# Revit family: Plumbing-Flushometer-Sloan-Valve-Sloan-186_
name_source: partatom
category: Plumbing Fixtures
units: mm (PartAtom-declared; Revit-internal decimal feet)

## family parameters
Cut with Voids When Loaded = No
Host = Face
OmniClass Number = 23.45.05.14.99
OmniClass Title = Other Sanitary Washing Plumbing Fixtures
Part Type = Normal
Room Calculation Point = No
Round Connector Dimension = Use Diameter
Shared = No

## types (22) — shared parameters
Assembly Code = D2020300
CW Connection = Yes
Centerline of Supply from Top of Fixture = 11 1/2"
Centerline of Supply to Centerline of Valve = 4 3/4"
Default Elevation = 0"
Edition number = 1
HW Connection = No
Height = 13 3/4"
Keynote = 15410
Manufacturer = Sloan Valve
Operating Water Pressure = 15 – 80 PSI (103 – 552 kPa)
Product Material = Sloan Valve - Finish - Polished Chrome
Product data url = https://bimobject.com
URL = www.sloanvalve.com
Valve Pressure Drop = 0.00 psi
Vent Connection = No
Waste Connection = No
Water Inlet Connection Diameter = 1"
zero-valued in all types: CWFU, HWFU, WFU

## per-type parameters (varying)
| type | Description | Flush Rate | Part Number |
| SLOAN 186-1.0-YJ | 1.0 gpf, Polished Chrome Finish, Fixture Connection Top Spud, Single Flush, Split Ring Pipe Support, Sloan® Exposed Manual Urinal Flushometer. | 1.0 gpf (3.8 Lpf) | 3782627 |
| SLOAN 186-1.0-YBC | 1.0 gpf, Cast Set Screw Wall Flange, Polished Chrome Finish, Fixture Connection Top Spud, Single Flush, Sloan® Exposed Manual Urinal Flushometer. | 1.0 gpf (3.8 Lpf) | 3782664 |
| SLOAN 186-1.0-YA | 1.0 gpf, Polished Chrome Finish, Fixture Connection Top Spud, Single Flush, Nickel-Silver Handle, Sloan® Exposed Manual Urinal Flushometer. | 1.0 gpf (3.8 Lpf) | 3782628 |
| SLOAN 186-1.0-XYV | 1.0 gpf, Polished Chrome Finish, Fixture Connection Top Spud, Single Flush, Less Vacuum Breaker, Sloan® Exposed Manual Urinal Flushometer. | 1.0 gpf (3.8 Lpf) | 3782642 |
| SLOAN 186-1.0-H-L | 1.0 gpf, Polished Chrome Finish, Fixture Connection Top Spud, Single Flush, Front of Valve Handle, Metal Index Push Button, Sloan® Exposed Manual Urinal Flushometer. | 1.0 gpf (3.8 Lpf) | 3782622 |
| SLOAN 186-1.0-H-2-OFST | 1.0 gpf, Polished Chrome Finish, Fixture Connection Top Spud, Single Flush, Front of Valve Handle, 2 Offset, Sloan® Exposed Manual Urinal Flushometer. | 1.0 gpf (3.8 Lpf) | 3782632 |
| SLOAN 186-0.5-XYV | 0.125 gpf, Dual-Filtered Bypass, Polished Chrome Finish, Fixture Connection Top Spud, Single Flush, Sloan® Exposed Manual Urinal Flushometer. | 0.5 gpf (1.9 Lpf) | 3782648 |
| SLOAN 186-0.125 | 0.125 gpf, Polished Chrome Finish, Fixture Connection Top Spud, Single Flush, Sloan® Exposed Manual Urinal Flushometer. | 0.125 gpf (0.5 Lpf) | 3782641 |
| SLOAN 186-1.0-SG | 1.0 gpf, Polished Chrome Finish, Fixture Connection Top Spud, Single Flush, Sanigard® Handle, Sloan® Exposed Manual Urinal Flushometer. | 1.0 gpf (3.8 Lpf) | 3782654 |
| SLOAN 186-1.5-DFB | 1.5 gpf, Dual-Filtered Fixed Bypass Diaphragm, Polished Chrome Finish, Fixture Connection Top Spud, Single Flush, Sloan® Exposed Manual Urinal Flushometer. | 1.5 gpf (5.7 Lpf) | 3782610 |
| SLOAN 186-0.125-DBP-SG | 0.125 gpf, Dual-Filtered Bypass, Polished Chrome Finish, Fixture Connection Top Spud, Single Flush, Sanigard® Handle, Sloan® Exposed Manual Urinal Flushometer. | 0.125 gpf (0.5 Lpf) | 3782644 |
| SLOAN 186-3.5 | 3.5 gpf, Polished Chrome Finish, Fixture Connection Top Spud, Single Flush, Sloan® Exposed Manual Urinal Flushometer. | 3.5 gpf (13.2 Lpf) | 3782660 |
| SLOAN 186-1.5 | 1.5 gpf, Polished Chrome Finish, Fixture Connection Top Spud, Single Flush, Sloan® Exposed Manual Urinal Flushometer. | 1.5 gpf (5.7 Lpf) | 3782600 |
| SLOAN 186-0.25-DBP | 0.25 gpf, Dual-Filtered Bypass, Polished Chrome Finish, Fixture Connection Top Spud, Single Flush, Sloan® Exposed Manual Urinal Flushometer. | 0.25 gpf (0.9 Lpf) | 3782661 |
| SLOAN 186-0.5-L/STOP | 0.5 gpf, Polished Chrome Finish, Fixture Connection Top Spud, Single Flush, Less Control Stop, Sloan® Exposed Manual Urinal Flushometer. | 0.5 gpf (1.9 Lpf) | 3782659 |
| SLOAN 186-1.0-DFB | 1.0 gpf, Dual-Filtered Fixed Bypass Diaphragm, Polished Chrome Finish, Fixture Connection Top Spud, Single Flush, Sloan® Exposed Manual Urinal Flushometer. | 1.0 gpf (3.8 Lpf) | 3782630 |
| SLOAN 186-0.5-DFB-SG | 0.5 gpf, Dual-Filtered Fixed Bypass Diaphragm, Polished Chrome Finish, Fixture Connection Top Spud, Single Flush, Sanigard® Handle, Sloan® Exposed Manual Urinal Flushometer. | 0.5 gpf (1.9 Lpf) | 3782663 |
| SLOAN 186-0.5-DFB - 2 | 0.5 gpf, Dual-Filtered Fixed Bypass Diaphragm, Polished Chrome Finish, Fixture Connection Top Spud, Single Flush, Sloan® Exposed Manual Urinal Flushometer. | 0.5 gpf (1.9 Lpf) | 3782666 |
| SLOAN 186-0.5-DFB - 1 | 0.5 gpf, Dual-Filtered Fixed Bypass Diaphragm, Polished Chrome Finish, Fixture Connection Top Spud, Single Flush, Sloan® Exposed Manual Urinal Flushometer. | 0.5 gpf (1.9 Lpf) | 3782666 |
| SLOAN 186-0.1 | 1.0 gpf, Polished Chrome Finish, Fixture Connection Top Spud, Single Flush, Sloan® Exposed Manual Urinal Flushometer. | 1.0 gpf (3.8 Lpf) | 3782624 |
| SLOAN 186-0.5 | 0.5 gpf, Polished Chrome Finish, Fixture Connection Top Spud, Single Flush, Sloan® Exposed Manual Urinal Flushometer. | 0.5 gpf (1.9 Lpf) | 3782655 |
| SLOAN 186-0.125-DBP | 0.125 gpf, Dual-Filtered Bypass, Polished Chrome Finish, Fixture Connection Top Spud, Single Flush, Sloan® Exposed Manual Urinal Flushometer. | 0.125 gpf (0.5 Lpf) | 3782643 |

note: column(s) folded — value = type name in every type: Model

## geometry (parser evidence)
native form markers: Sweep x9
no freeform markers — native parametric forms only
